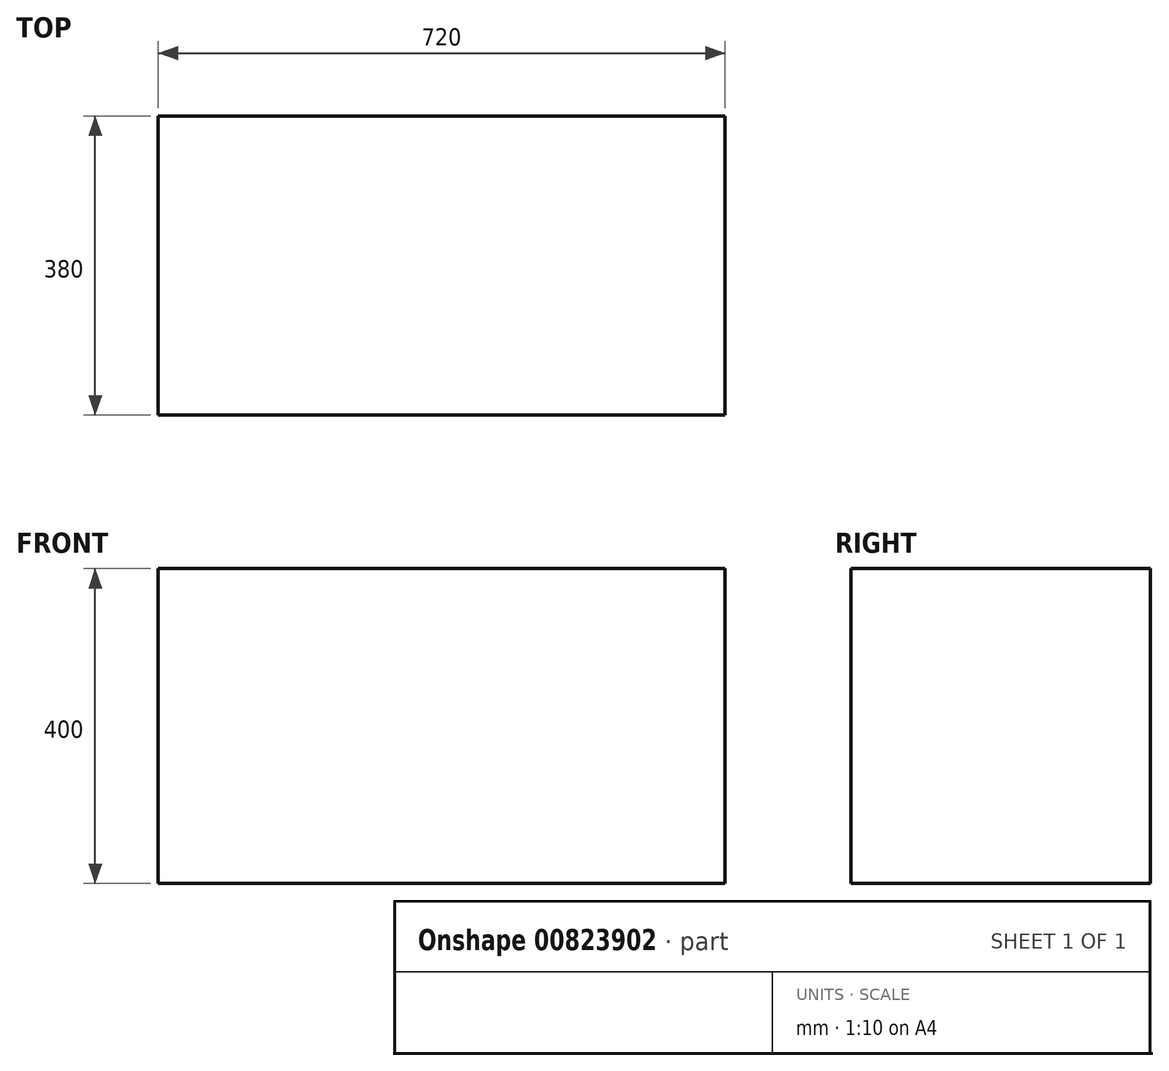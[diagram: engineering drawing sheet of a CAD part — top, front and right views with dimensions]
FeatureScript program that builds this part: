
annotation { "Feature Type Name" : "Feature", "Feature Type Description" : "" }
export const myFeature = defineFeature(function(context is Context, id is Id, definition is map)
    precondition{}
    {
        {
            var Q0;
            Q0=qCreatedBy(makeId("Front.planeOp"),FACE);
            var sketch = newSketch(context, id + "F0", { "sketchPlane" : qUnion([Q0])});
            skLineSegment(sketch, "E0.bottom", {"start": v(0, 0) * mm, "end": v(720, 0) * mm});
            skLineSegment(sketch, "E0.top", {"start": v(0, 400) * mm, "end": v(720, 400) * mm});
            skLineSegment(sketch, "E0.left", {"start": v(0, 0) * mm, "end": v(0, 400) * mm});
            skLineSegment(sketch, "E0.right", {"start": v(720, 0) * mm, "end": v(720, 400) * mm});
            skSolve(sketch);
        }
        {
            var Q0;
            Q0=makeQuery(id+"F0.imprint","IMPRINT",FACE,{"disambiguationData":[TD([[makeQuery(id+"F0.imprint","IMPRINT",EDGE,{"derivedFrom":sQuery(id+"F0.wireOp",EDGE,"E0.bottom")}),1.0]])]});
            extrude(context, id + "F1", {"entities" : qUnion([Q0]), "endBound" : BoundingType.SYMMETRIC, "depth" : 380 * mm, "offsetDistance" : 25 * mm});
        }
    });
